# Revit family: Урна 126
name_source: partatom
category: Антураж
revit_build: Autodesk Revit 2017 (Build: 20160225_1515(x64)
units: mm (PartAtom-declared; Revit-internal decimal feet)

## family parameters
Всегда вертикально = Да
Источник визуального образа = Геометрия семейства
На основе рабочей плоскости = Нет
Общий = Нет
При загрузке вырезать с полостями = Нет
Точка расчета площади = Нет

## types (13) — shared parameters
ADSK_Код изделия = 7324
ADSK_Материал урны = Черный
ADSK_Наименование = Урна 126
ADSK_Объем = 0.03 м³
ADSK_Размер_Высота = 998 мм
ADSK_Размер_Диаметр = 340 мм
ADSK_Размер_Ширина = 370 мм
URL = https://hobbyka.ru
Изготовитель = ООО "Хоббика"
Стоимость = 2200 $

## per-type parameters (varying)
| type | Высота | Материал ведра |
| Урна 126 (зеленый) | 998 мм | Зелёный RAL6029 |
| Урна 126 (салатовый) | 998 мм | Салатовый RAL6018 |
| Урна 126 (красный) | 0 мм | Красный RAL3020 |
| Урна 126 (бордо) | 998 мм | Бордо RAL3004 |
| Урна 126 (синий) | 998 мм | Синий RAL5002 |
| Урна 126 (светло-серый) | 998 мм | Светло-серый RAL7035 |
| Урна 126 (темно-серый) | 998 мм | Темно-серый RAL7040 |
| Урна 126 (темный шоколад) | 998 мм | Темный шоколад |
| Урна 126 (черный) | 998 мм | Черный |
| Урна 126 (оранжевый) | 998 мм | Оранжевый RAL2008 |
| Урна 126 (антик серебро) | 998 мм | Антик серебро |
| Урна 126 (антик медь) | 998 мм | Антик медь |
| Урна 126 (антик бронза) | 998 мм | Антик бронза |
